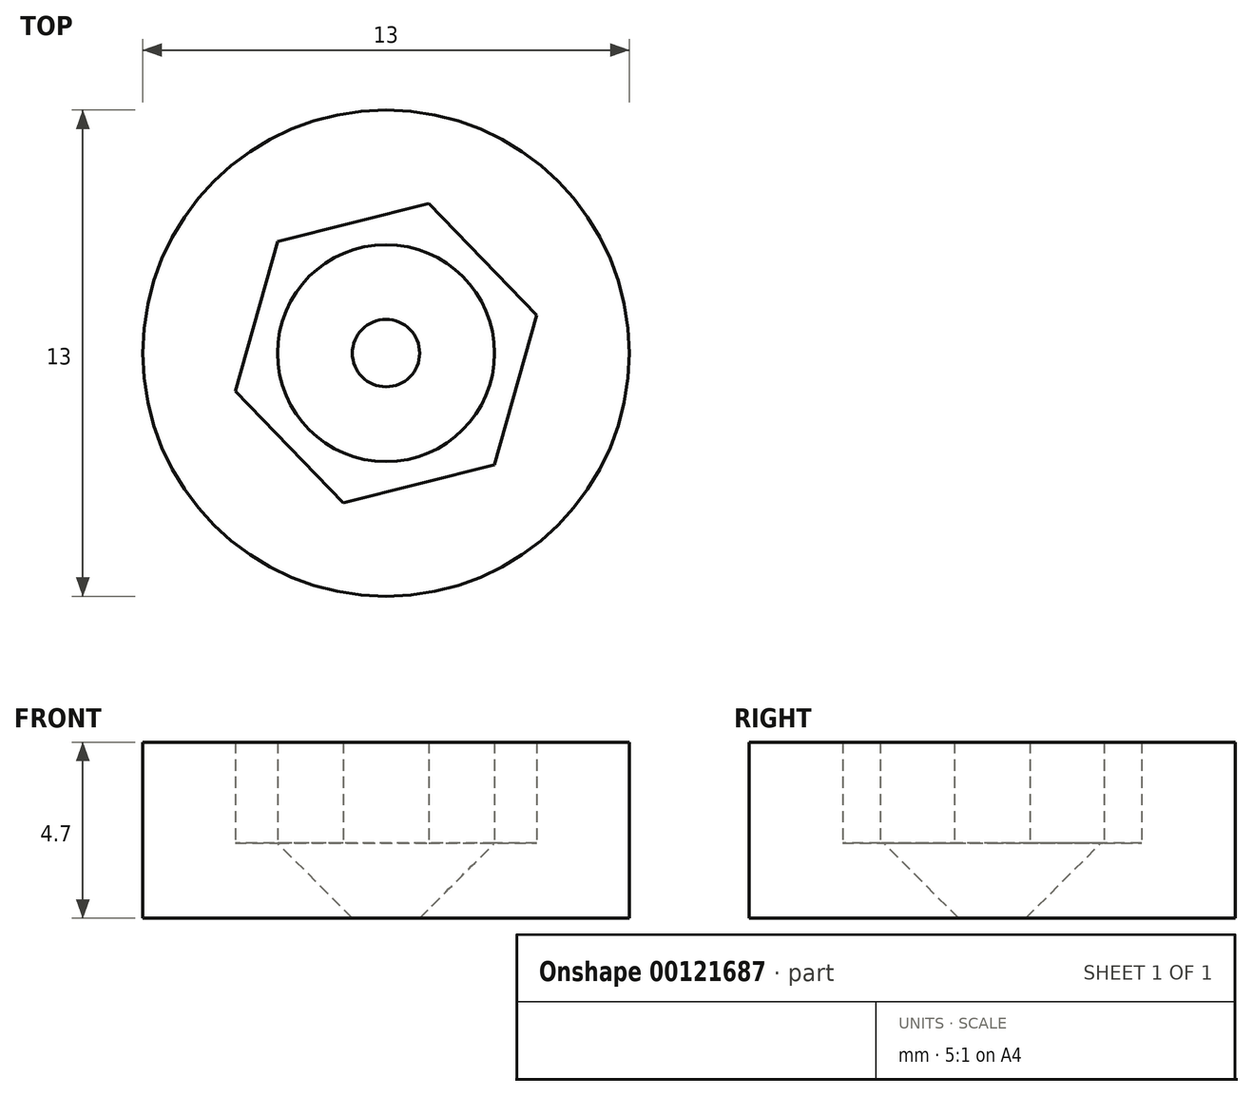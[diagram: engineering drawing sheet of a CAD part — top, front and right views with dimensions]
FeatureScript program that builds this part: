
annotation { "Feature Type Name" : "Feature", "Feature Type Description" : "" }
export const myFeature = defineFeature(function(context is Context, id is Id, definition is map)
    precondition{}
    {
        {
            var Q0;
            Q0=qCreatedBy(makeId("Top.planeOp"),FACE);
            var sketch = newSketch(context, id + "F0", { "sketchPlane" : qUnion([Q0])});
            skCircle(sketch, "E0", {"center": v(0, 0) * mm, "radius": 6.5 * mm});
            skCircle(sketch, "E1", {"center": v(0, 0) * mm, "radius": 0.9 * mm});
            skSolve(sketch);
        }
        {
            var Q0;
            Q0=makeQuery(id+"F0.imprint","IMPRINT",FACE,{"disambiguationData":[TD([[makeQuery(id+"F0.imprint","IMPRINT",EDGE,{"derivedFrom":sQuery(id+"F0.wireOp",EDGE,"E0")}),1.0]])]});
            extrude(context, id + "F1", {"entities" : qUnion([Q0]), "depth" : 2 * mm});
        }
        {
            var Q0;
            Q0=makeQuery(id+"F1.opExtrude","CAP_EDGE",EDGE,{"disambiguationData":[OSD([sQuery(id+"F0.wireOp",EDGE,"E1")])],"isStart":false});
            chamfer(context, id + "F2", {"entities" : qUnion([Q0]), "width" : 2 * mm, "tangentPropagation" : true});
        }
        {
            var Q0;
            Q0=makeQuery(id+"F1.opExtrude","CAP_FACE",FACE,{"disambiguationData":[OSD([sQuery(id+"F0.wireOp",EDGE,"E0"),sQuery(id+"F0.wireOp",EDGE,"E1")])],"isStart":false});
            var sketch = newSketch(context, id + "F3", { "sketchPlane" : qUnion([Q0])});
            skCircle(sketch, "E2.cCircle", {"center": v(0, 0) * mm, "radius": 3.6 * mm, "construction": true});
            skLineSegment(sketch, "E2.0", {"start": v(1.14, 4) * mm, "end": v(4.03, 1.01) * mm});
            skLineSegment(sketch, "E2.1", {"start": v(4.03, 1.01) * mm, "end": v(2.9, -2.99) * mm});
            skLineSegment(sketch, "E2.2", {"start": v(2.9, -2.99) * mm, "end": v(-1.14, -4) * mm});
            skLineSegment(sketch, "E2.3", {"start": v(-1.14, -4) * mm, "end": v(-4.03, -1.01) * mm});
            skLineSegment(sketch, "E2.4", {"start": v(-4.03, -1.01) * mm, "end": v(-2.9, 2.99) * mm});
            skLineSegment(sketch, "E2.5", {"start": v(-2.9, 2.99) * mm, "end": v(1.14, 4) * mm});
            skPoint(sketch, "E2.0.midPoint", {"position": v(2.59, 2.5) * mm});
            skCircle(sketch, "E3", {"center": v(0, 0) * mm, "radius": 6.5 * mm});
            skSolve(sketch);
        }
        {
            var Q0;
            Q0 = qSketchRegion(id + "F3", true);
            var Q1;
            Q1=makeQuery(id+"F3.imprint","IMPRINT",FACE,{"disambiguationData":[TD([[makeQuery(id+"F3.imprint","IMPRINT",EDGE,{"derivedFrom":sQuery(id+"F3.wireOp",EDGE,"E2.0")}),1.0]])]});
            extrude(context, id + "F4", {"entities" : qUnion([Q0, Q1]), "operationType" : NewBodyOperationType.ADD, "depth" : 2.7 * mm});
        }
    });
